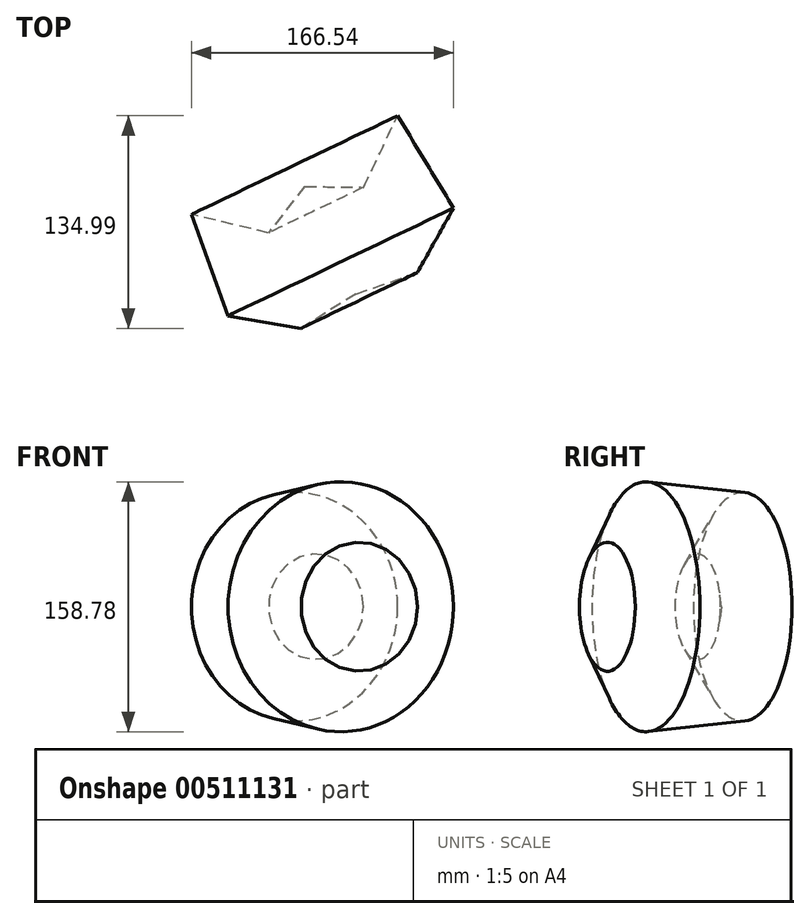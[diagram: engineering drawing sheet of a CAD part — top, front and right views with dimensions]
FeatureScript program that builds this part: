
annotation { "Feature Type Name" : "Feature", "Feature Type Description" : "" }
export const myFeature = defineFeature(function(context is Context, id is Id, definition is map)
    precondition{}
    {
        {
            var Q0;
            Q0=qCreatedBy(makeId("Top.planeOp"),FACE);
            var sketch = newSketch(context, id + "F0", { "sketchPlane" : qUnion([Q0])});
            skLineSegment(sketch, "E0", {"start": v(-54.21, 38.04) * mm, "end": v(-30.9, -26.38) * mm});
            skLineSegment(sketch, "E1", {"start": v(-30.9, -26.38) * mm, "end": v(15.45, -34.25) * mm});
            skLineSegment(sketch, "E2", {"start": v(15.45, -34.25) * mm, "end": v(50.43, -12.39) * mm});
            skLineSegment(sketch, "E3", {"start": v(50.43, -12.39) * mm, "end": v(17.78, 55.82) * mm});
            skLineSegment(sketch, "E4", {"start": v(17.78, 55.82) * mm, "end": v(-5.25, 26.38) * mm});
            skLineSegment(sketch, "E5", {"start": v(-54.21, 38.04) * mm, "end": v(-5.25, 26.38) * mm});
            skSolve(sketch);
        }
        {
            var Q0;
            Q0=makeQuery(id+"F0.imprint","IMPRINT",FACE,{"disambiguationData":[TD([[makeQuery(id+"F0.imprint","IMPRINT",EDGE,{"derivedFrom":sQuery(id+"F0.wireOp",EDGE,"E0")}),1.0]])]});
            var Q1;
            Q1=sQuery(id+"F0.wireOp",EDGE,"E3");
            revolve(context, id + "F1", {"entities" : qUnion([Q0]), "axis" : qUnion([Q1]), "revolveType" : RevolveType.FULL});
        }
    });
